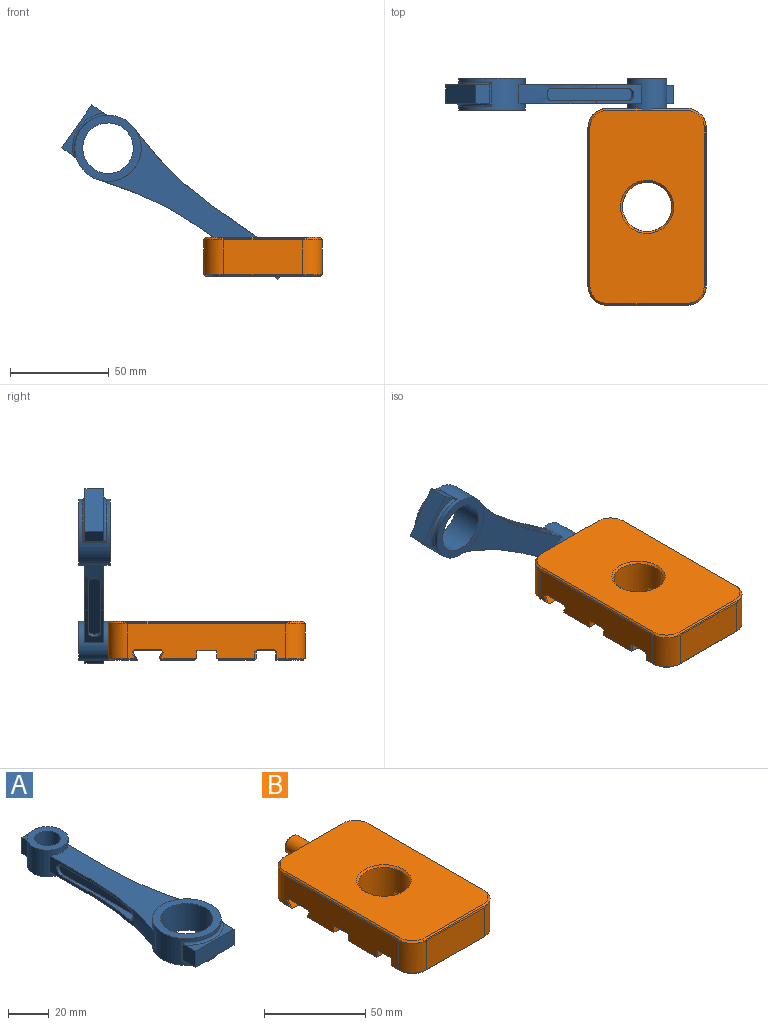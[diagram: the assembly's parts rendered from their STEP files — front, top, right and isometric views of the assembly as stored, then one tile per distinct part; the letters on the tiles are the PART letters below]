
ASSEMBLY  parts=2 mates=1
PART A: 38 faces, bbox 33.7x129.1x16.1 mm
  f0: plane 10x4mm, normal (0,0,1), area 30.9mm2, adj f11,f12,f13,f31
  f1: plane 10x4mm, normal (0,0,-1), area 30.9mm2, adj f11,f12,f13,f31
  f2: plane 82.69x31.66mm, normal (0,0,1), area 1120mm2, adj f4,f5,f6,f13,f28,f29
  f3: plane 82.69x31.66mm, normal (0,0,-1), area 1120mm2, adj f4,f5,f6,f13,f28,f29
  f4: plane 28x9.6mm, normal (-1,0,0), area 126.7mm2, adj f2,f3,f5,f13,f21,f22,f26
  f5: cylinder r=163.3mm len=54.69mm, axis (0,0,-1), area 326.4mm2, adj f2,f3,f4,f6,f21,f22,f27
  f6: cylinder r=16.8mm len=33.6mm, axis (0,0,-1), area 914.8mm2, adj f2,f3,f5,f16,f17,f23,f24,f25
  f7: plane 10.6x8.74mm, normal (-1,0,0), area 83.7mm2, adj f8,f14,f15,f23,f24,f25
  f8: plane 26.6x9.6mm, normal (0,-1,0), area 255.4mm2, adj f7,f14,f15,f30
  f9: cylinder r=12.8mm len=25.6mm, axis (0,0,-1), area 1286.8mm2, adj f16,f17
  f10: cylinder r=6.25mm len=16mm, axis (0,0,-1), area 628.3mm2, adj f18,f19
  f11: plane 10x9.6mm, normal (0,1,0), area 96mm2, adj f0,f1,f12,f31
  f12: plane 9.6x4mm, normal (-1,0,0), area 38.4mm2, adj f0,f1,f11,f13
  f13: cylinder r=10mm len=20mm, axis (0,0,-1), area 771.4mm2, adj f0,f1,f2,f3,f4,f12,f18,f19
  f14: plane 26.6x7.21mm, normal (0,0,1), area 83.7mm2, adj f7,f8,f23,f30
  f15: plane 26.6x7.21mm, normal (0,0,-1), area 83.7mm2, adj f7,f8,f24,f30
  f16: plane 33.6x33.6mm, normal (0,0,-1), area 372mm2, adj f6,f9
  f17: plane 33.6x33.6mm, normal (0,0,1), area 372mm2, adj f6,f9
  f18: plane 20x20mm, normal (0,0,-1), area 191.4mm2, adj f10,f13
  f19: plane 20x20mm, normal (0,0,1), area 191.4mm2, adj f10,f13
  f20: plane 56x6.4mm, normal (-1,0,0), area 349.6mm2, adj f21,f22,f26,f27
  f21: plane 49.6x4.36mm, normal (0,0,1), area 106.8mm2, adj f4,f5,f20,f26,f27
  f22: plane 49.6x4.36mm, normal (0,0,-1), area 106.8mm2, adj f4,f5,f20,f26,f27
  f23: torus R=18mm, axis (0,0,1), area 57.5mm2, adj f6,f7,f14,f25,f30,f35
  f24: torus R=18mm, axis (0,0,1), area 57.5mm2, adj f6,f7,f15,f25,f30,f35
  f25: cylinder r=1.2mm len=12mm, axis (0,0,-1), area 8.6mm2, adj f6,f7,f23,f24
  f26: cylinder r=3.2mm len=6.4mm, axis (-1,0,0), area 16.1mm2, adj f4,f20,f21,f22
  f27: cylinder r=3.2mm len=6.4mm, axis (1,0,0), area 47.8mm2, adj f5,f20,f21,f22
  f28: plane 28x9.6mm, normal (1,0,0), area 126.7mm2, adj f2,f3,f13,f29,f33,f34,f36
  f29: cylinder r=163.3mm len=54.69mm, axis (0,0,-1), area 326.4mm2, adj f2,f3,f6,f28,f33,f34,f37
  f30: plane 10.6x8.74mm, normal (1,0,0), area 83.7mm2, adj f8,f14,f15,f23,f24,f35
  f31: plane 9.6x4mm, normal (1,0,0), area 38.4mm2, adj f0,f1,f11,f13
  f32: plane 56x6.4mm, normal (1,0,0), area 349.6mm2, adj f33,f34,f36,f37
  f33: plane 49.6x4.36mm, normal (0,0,1), area 106.8mm2, adj f28,f29,f32,f36,f37
  f34: plane 49.6x4.36mm, normal (0,0,-1), area 106.8mm2, adj f28,f29,f32,f36,f37
  f35: cylinder r=1.2mm len=12mm, axis (0,0,-1), area 8.6mm2, adj f6,f23,f24,f30
  f36: cylinder r=3.2mm len=6.4mm, axis (1,0,0), area 16.1mm2, adj f28,f32,f33,f34
  f37: cylinder r=3.2mm len=6.4mm, axis (-1,0,0), area 47.8mm2, adj f29,f32,f33,f34
PART B: 96 faces, bbox 60x115x20.4 mm
  f0: plane 80x17.59mm, normal (1,0,0), area 1251.3mm2, adj f10,f11,f12,f29,f32,f37,f53,f58
  f1: plane 80x17.59mm, normal (-1,0,0), area 1251.3mm2, adj f13,f14,f15,f30,f31,f33,f38,f54
  f2: plane 58x17.27mm, normal (0,0,-1), area 871.8mm2, adj f59,f60,f61,f62,f63,f64
  f3: plane 58x18mm, normal (0,0,-1), area 914.2mm2, adj f65,f66,f67,f68,f69,f70
  f4: plane 58x14mm, normal (0,0,-1), area 777.2mm2, adj f17,f33,f34,f35,f36,f37
  f5: plane 40x17.59mm, normal (0,1,0), area 624.9mm2, adj f22,f29,f30,f45,f56
  f6: plane 40x17.59mm, normal (0,-1,0), area 703.4mm2, adj f31,f32,f35,f46
  f7: cylinder r=12.5mm len=25mm, axis (0,0,1), area 1331.4mm2, adj f10,f11,f12,f13,f14,f15,f24,f61
  f8: plane 58x14mm, normal (0,0,-1), area 777.2mm2, adj f21,f54,f55,f56,f57,f58
  f9: plane 98x58mm, normal (0,0,1), area 5041.9mm2, adj f24,f25,f26,f27,f28,f41,f42,f49
  f10: plane 18.54x4mm, normal (0,1,0), area 74.2mm2, adj f0,f7,f12,f69
  f11: plane 18.54x4mm, normal (0,-1,0), area 74.2mm2, adj f0,f7,f12,f59
  f12: plane 18.54x10mm, normal (0,0,-1), area 178.4mm2, adj f0,f7,f10,f11
  f13: plane 18.54x4mm, normal (0,1,0), area 74.2mm2, adj f1,f7,f15,f68
  f14: plane 18.54x4mm, normal (0,-1,0), area 74.2mm2, adj f1,f7,f15,f63
  f15: plane 18.54x10mm, normal (0,0,-1), area 178.4mm2, adj f1,f7,f13,f14
  f16: plane 58.85x3.42mm, normal (0,-1,0), area 201.4mm2, adj f65,f77,f81,f83
  f17: plane 58.85x4.42mm, normal (0,1,0), area 260.1mm2, adj f4,f33,f37,f72,f74,f75
  f18: plane 58.85x8.85mm, normal (0,0,-1), area 520.5mm2, adj f75,f76,f80,f81
  f19: plane 58.85x2.63mm, normal (0,0.87,0.5), area 179mm2, adj f62,f89,f93,f95
  f20: plane 58.85x13.77mm, normal (0,0,-1), area 810.5mm2, adj f87,f88,f92,f93
  f21: plane 58.85x4.13mm, normal (0,-0.87,0.5), area 280.7mm2, adj f8,f54,f58,f84,f86,f87
  f22: cylinder r=5mm len=14mm, axis (0,-1,0), area 439.8mm2, adj f5,f71
  f23: plane 8x8mm, normal (0,1,0), area 50.3mm2, adj f71
  f24: cone r=12.5mm half-angle=45deg, axis (0,0,1), area 115.5mm2, adj f7,f9
  f25: plane 80x0.71mm, normal (0.71,0,0.71), area 80mm2, adj f9,f49,f50,f53
  f26: plane 40x0.71mm, normal (0,0.71,0.71), area 40mm2, adj f9,f41,f45,f49
  f27: plane 40x0.71mm, normal (0,-0.71,0.71), area 40mm2, adj f9,f42,f46,f50
  f28: plane 80x0.71mm, normal (-0.71,0,0.71), area 80mm2, adj f9,f38,f41,f42
  f29: cylinder r=10mm len=18mm, axis (0,0,-1), area 281.5mm2, adj f0,f5,f47,f49,f51,f57
  f30: cylinder r=10mm len=18mm, axis (0,0,1), area 281.5mm2, adj f1,f5,f39,f41,f43,f55
  f31: cylinder r=10mm len=18mm, axis (0,0,-1), area 281.5mm2, adj f1,f6,f34,f40,f42,f44
  f32: cylinder r=10mm len=18mm, axis (0,0,1), area 281.5mm2, adj f0,f6,f36,f48,f50,f52
  f33: plane 5x1mm, normal (-0.71,0,-0.71), area 6.8mm2, adj f1,f4,f17,f34,f74
  f34: cone r=9mm half-angle=45deg, axis (0,0,1), area 21.1mm2, adj f4,f31,f33,f35
  f35: plane 40x1mm, normal (0,-0.71,-0.71), area 56.6mm2, adj f4,f6,f34,f36
  f36: cone r=9mm half-angle=45deg, axis (0,0,1), area 21.1mm2, adj f4,f32,f35,f37
  f37: plane 5x1mm, normal (0.71,0,-0.71), area 6.8mm2, adj f0,f4,f17,f36,f72
  f38: plane 80x0.71mm, normal (-0.92,0,0.38), area 61.2mm2, adj f1,f28,f39,f40
  f39: bspline ~3x1.12mm, area 1.1mm2, adj f30,f38,f41
  f40: bspline ~3x1.12mm, area 1.1mm2, adj f31,f38,f42
  f41: cone r=9mm half-angle=45deg, axis (0,0,-1), area 19.9mm2, adj f9,f26,f28,f30,f39,f43
  f42: cone r=9mm half-angle=45deg, axis (0,0,-1), area 19.9mm2, adj f9,f27,f28,f31,f40,f44
  f43: bspline ~4.75x1.79mm, area 1.1mm2, adj f30,f41,f45
  f44: bspline ~4.75x1.79mm, area 1.1mm2, adj f31,f42,f46
  f45: plane 40x0.71mm, normal (0,0.92,0.38), area 30.6mm2, adj f5,f26,f43,f47
  f46: plane 40x0.71mm, normal (0,-0.92,0.38), area 30.6mm2, adj f6,f27,f44,f48
  f47: bspline ~3x1.12mm, area 1.1mm2, adj f29,f45,f49
  f48: bspline ~3x1.12mm, area 1.1mm2, adj f32,f46,f50
  f49: cone r=9mm half-angle=45deg, axis (0,0,-1), area 19.9mm2, adj f9,f25,f26,f29,f47,f51
  f50: cone r=9mm half-angle=45deg, axis (0,0,-1), area 19.9mm2, adj f9,f25,f27,f32,f48,f52
  f51: bspline ~3x1.12mm, area 1.1mm2, adj f29,f49,f53
  f52: bspline ~3x1.12mm, area 1.1mm2, adj f32,f50,f53
  f53: plane 80x0.71mm, normal (0.92,0,0.38), area 61.2mm2, adj f0,f25,f51,f52
  f54: plane 5x1mm, normal (-0.71,0,-0.71), area 6.4mm2, adj f1,f8,f21,f55,f84
  f55: cone r=9mm half-angle=45deg, axis (0,0,1), area 21.1mm2, adj f8,f30,f54,f56
  f56: plane 40x1mm, normal (0,0.71,-0.71), area 56.6mm2, adj f5,f8,f55,f57
  f57: cone r=9mm half-angle=45deg, axis (0,0,1), area 21.1mm2, adj f8,f29,f56,f58
  f58: plane 5x1mm, normal (0.71,0,-0.71), area 6.4mm2, adj f0,f8,f21,f57,f86
  f59: plane 18.56x1.02mm, normal (0,-0.71,-0.71), area 25.1mm2, adj f2,f11,f60,f61
  f60: plane 18.82x1mm, normal (0.71,0,-0.71), area 25.5mm2, adj f0,f2,f59,f62,f95
  f61: cone r=13.5mm half-angle=45deg, axis (0,0,-1), area 41.7mm2, adj f2,f7,f59,f63
  f62: plane 59.92x1.5mm, normal (0,0.87,-0.5), area 102.4mm2, adj f2,f19,f60,f64,f89,f95
  f63: plane 18.56x1.02mm, normal (0,-0.71,-0.71), area 25.1mm2, adj f2,f14,f61,f64
  f64: plane 18.82x1mm, normal (-0.71,0,-0.71), area 25.5mm2, adj f1,f2,f62,f63,f89
  f65: plane 59.42x1mm, normal (0,-0.71,-0.71), area 83.2mm2, adj f3,f16,f66,f67,f77,f83
  f66: plane 19.71x1mm, normal (-0.71,0,-0.71), area 26.8mm2, adj f1,f3,f65,f68,f83
  f67: plane 19.71x1mm, normal (0.71,0,-0.71), area 26.8mm2, adj f0,f3,f65,f69,f77
  f68: plane 18.56x1.02mm, normal (0,0.71,-0.71), area 25.1mm2, adj f3,f13,f66,f70
  f69: plane 18.56x1.02mm, normal (0,0.71,-0.71), area 25.1mm2, adj f3,f10,f67,f70
  f70: cone r=13.5mm half-angle=45deg, axis (0,0,-1), area 41.7mm2, adj f3,f7,f68,f69
  f71: cone r=4mm half-angle=45deg, axis (0,-1,0), area 40mm2, adj f22,f23
  f72: plane 4x0.58mm, normal (0.71,0.71,0), area 3mm2, adj f0,f17,f37,f73
  f73: plane 1.15x1.15mm, normal (0.58,0.58,-0.58), area 0.9mm2, adj f0,f72,f75,f76
  f74: plane 4x0.58mm, normal (-0.71,0.71,0), area 3mm2, adj f1,f17,f33,f78
  f75: plane 58.85x0.58mm, normal (0,0.71,-0.71), area 48mm2, adj f17,f18,f73,f78
  f76: plane 8.85x0.58mm, normal (0.71,0,-0.71), area 7.2mm2, adj f0,f18,f73,f79
  f77: plane 3.71x0.58mm, normal (0.71,-0.71,0), area 2.9mm2, adj f0,f16,f65,f67,f79
  f78: plane 1.15x1.15mm, normal (-0.58,0.58,-0.58), area 0.9mm2, adj f1,f74,f75,f80
  f79: plane 1.15x1.15mm, normal (0.58,-0.58,-0.58), area 0.9mm2, adj f0,f76,f77,f81
  f80: plane 8.85x0.58mm, normal (-0.71,0,-0.71), area 7.2mm2, adj f1,f18,f78,f82
  f81: plane 58.85x0.58mm, normal (0,-0.71,-0.71), area 48mm2, adj f16,f18,f79,f82
  f82: plane 1.15x1.15mm, normal (-0.58,-0.58,-0.58), area 0.9mm2, adj f1,f80,f81,f83
  f83: plane 3.71x0.58mm, normal (-0.71,-0.71,0), area 2.9mm2, adj f1,f16,f65,f66,f82
  f84: plane 3.71x2.64mm, normal (-0.71,-0.61,0.35), area 3.1mm2, adj f1,f21,f54,f85
  f85: plane 1.73x1mm, normal (-0.45,-0.77,-0.45), area 1mm2, adj f1,f84,f87,f88
  f86: plane 3.71x2.64mm, normal (0.71,-0.61,0.35), area 3.1mm2, adj f0,f21,f58,f90
  f87: plane 58.85x0.87mm, normal (0,-0.87,-0.5), area 58.8mm2, adj f20,f21,f85,f90
  f88: plane 13.77x0.58mm, normal (-0.71,0,-0.71), area 11.2mm2, adj f1,f20,f85,f91
  f89: plane 3.17x2.02mm, normal (-0.71,0.61,0.35), area 2.6mm2, adj f1,f19,f62,f64,f91
  f90: plane 1.73x1mm, normal (0.45,-0.77,-0.45), area 1mm2, adj f0,f86,f87,f92
  f91: plane 1.73x1mm, normal (-0.45,0.77,-0.45), area 1mm2, adj f1,f88,f89,f93
  f92: plane 13.77x0.58mm, normal (0.71,0,-0.71), area 11.2mm2, adj f0,f20,f90,f94
  f93: plane 58.85x0.87mm, normal (0,0.87,-0.5), area 58.8mm2, adj f19,f20,f91,f94
  f94: plane 1.73x1mm, normal (0.45,0.77,-0.45), area 1mm2, adj f0,f92,f93,f95
  f95: plane 3.17x2.02mm, normal (0.71,0.61,0.35), area 2.6mm2, adj f0,f19,f60,f62,f94
PLACE A rot(axis=(0.35,0.66,-0.66),141.9deg) t=(-122.42,117.01,70.88)mm
PLACE B t=(-43.77,60.01,25.83)mm fixed
MATE revolute B.f22 <-> A.f10  axis (0,1,0) through (-43.77,125.01,15.83)mm
